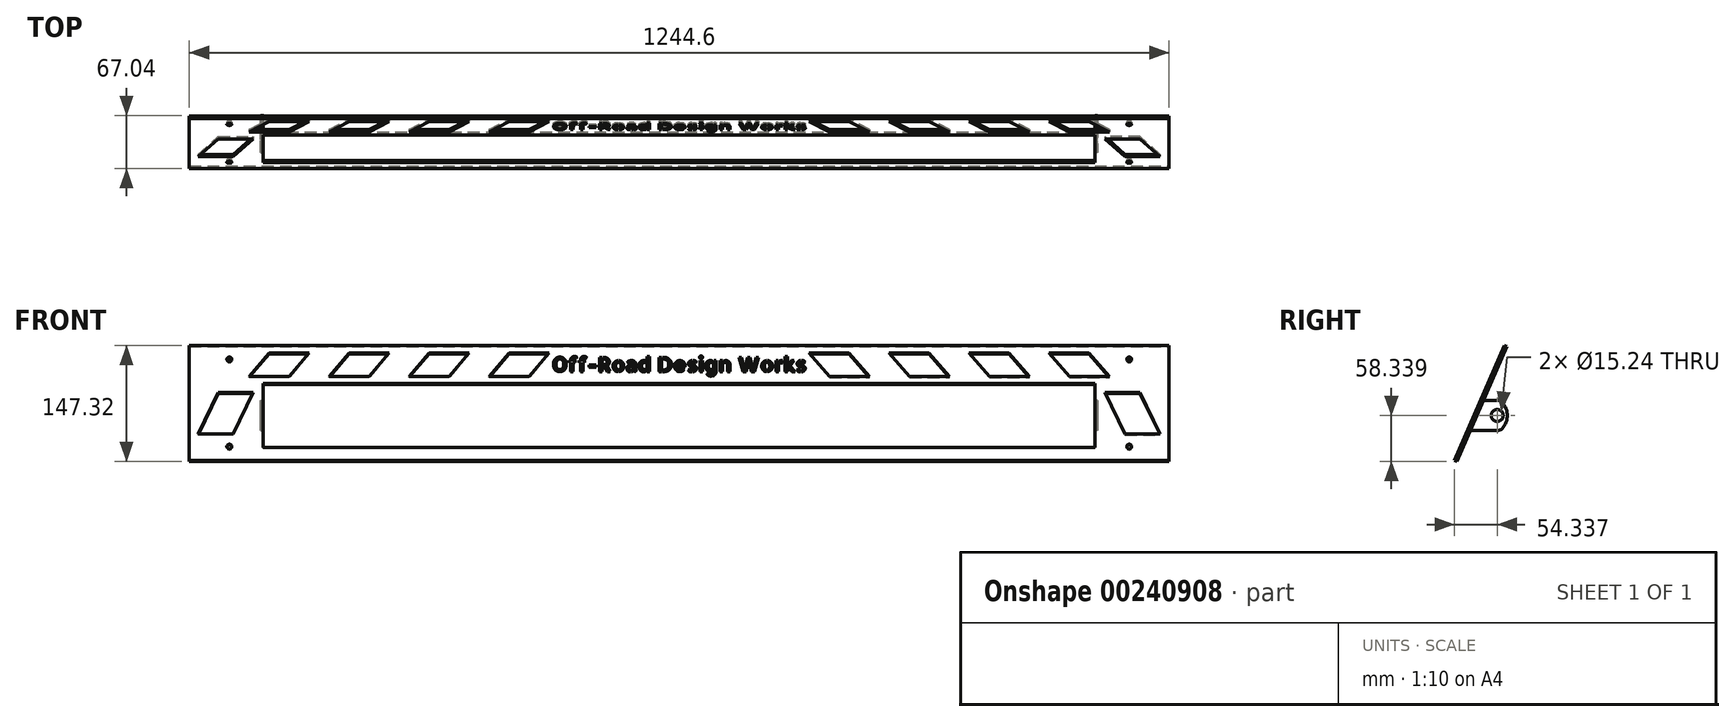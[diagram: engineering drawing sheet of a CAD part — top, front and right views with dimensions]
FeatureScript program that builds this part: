
annotation { "Feature Type Name" : "Feature", "Feature Type Description" : "" }
export const myFeature = defineFeature(function(context is Context, id is Id, definition is map)
    precondition{}
    {
        {
            var Q0;
            Q0=qCreatedBy(makeId("Right.planeOp"),FACE);
            var sketch = newSketch(context, id + "F0", { "sketchPlane" : qUnion([Q0])});
            skLineSegment(sketch, "E0", {"start": v(0, 0) * mm, "end": v(63.5, 146.05) * mm});
            skLineSegment(sketch, "E1", {"start": v(63.5, 146.05) * mm, "end": v(66.41, 144.78) * mm});
            skLineSegment(sketch, "E2", {"start": v(66.41, 144.78) * mm, "end": v(2.91, -1.27) * mm});
            skLineSegment(sketch, "E3", {"start": v(2.91, -1.27) * mm, "end": v(0, 0) * mm});
            skSolve(sketch);
        }
        {
            var Q0;
            Q0 = qSketchRegion(id + "F0", true);
            extrude(context, id + "F1", {"entities" : qUnion([Q0]), "oppositeDirection" : true, "depth" : 622.3 * mm, "hasSecondDirection" : true, "secondDirectionOppositeDirection" : false, "secondDirectionDepth" : 622.3 * mm});
        }
        {
            var Q0;
            Q0=makeQuery(id+"F1.opExtrude","SWEPT_FACE",FACE,{"disambiguationData":[OSD([sQuery(id+"F0.wireOp",EDGE,"E0")])]});
            var sketch = newSketch(context, id + "F2", { "sketchPlane" : qUnion([Q0])});
            skLineSegment(sketch, "E4", {"start": v(0, 0) * mm, "end": v(0, 463.2) * mm, "construction": true});
            skLineSegment(sketch, "E5", {"start": v(0, 106.68) * mm, "end": v(-528.32, 106.68) * mm});
            skLineSegment(sketch, "E6", {"start": v(-528.32, 106.68) * mm, "end": v(-528.32, 17.78) * mm});
            skLineSegment(sketch, "E7", {"start": v(-528.32, 17.78) * mm, "end": v(0, 17.78) * mm});
            skLineSegment(sketch, "E8.MirrorCS", {"start": v(0, 106.68) * mm, "end": v(528.32, 106.68) * mm});
            skLineSegment(sketch, "E9.MirrorCS", {"start": v(528.32, 106.68) * mm, "end": v(528.32, 17.78) * mm});
            skLineSegment(sketch, "E10.MirrorCS", {"start": v(528.32, 17.78) * mm, "end": v(0, 17.78) * mm});
            skLineSegment(sketch, "E11", {"start": v(165.1, 149.1) * mm, "end": v(215.9, 149.1) * mm});
            skLineSegment(sketch, "E12", {"start": v(215.9, 149.1) * mm, "end": v(241.7, 116.08) * mm});
            skLineSegment(sketch, "E13", {"start": v(241.7, 116.08) * mm, "end": v(190.9, 116.08) * mm});
            skLineSegment(sketch, "E14", {"start": v(190.9, 116.08) * mm, "end": v(165.1, 149.1) * mm});
            skLineSegment(sketch, "E15.1.0.0", {"start": v(317.5, 149.1) * mm, "end": v(343.3, 116.08) * mm});
            skLineSegment(sketch, "E15.1.0.1", {"start": v(343.3, 116.08) * mm, "end": v(292.5, 116.08) * mm});
            skLineSegment(sketch, "E15.1.0.2", {"start": v(266.7, 149.1) * mm, "end": v(317.5, 149.1) * mm});
            skLineSegment(sketch, "E15.1.0.3", {"start": v(292.5, 116.08) * mm, "end": v(266.7, 149.1) * mm});
            skLineSegment(sketch, "E15.2.0.0", {"start": v(419.1, 149.1) * mm, "end": v(444.9, 116.08) * mm});
            skLineSegment(sketch, "E15.2.0.1", {"start": v(444.9, 116.08) * mm, "end": v(394.1, 116.08) * mm});
            skLineSegment(sketch, "E15.2.0.2", {"start": v(368.3, 149.1) * mm, "end": v(419.1, 149.1) * mm});
            skLineSegment(sketch, "E15.2.0.3", {"start": v(394.1, 116.08) * mm, "end": v(368.3, 149.1) * mm});
            skLineSegment(sketch, "E15.3.0.0", {"start": v(520.7, 149.1) * mm, "end": v(546.5, 116.08) * mm});
            skLineSegment(sketch, "E15.3.0.1", {"start": v(546.5, 116.08) * mm, "end": v(495.7, 116.08) * mm});
            skLineSegment(sketch, "E15.3.0.2", {"start": v(469.9, 149.1) * mm, "end": v(520.7, 149.1) * mm});
            skLineSegment(sketch, "E15.3.0.3", {"start": v(495.7, 116.08) * mm, "end": v(469.9, 149.1) * mm});
            skLineSegment(sketch, "E15.direction1", {"start": v(215.9, 149.1) * mm, "end": v(317.5, 149.1) * mm, "construction": true});
            skLineSegment(sketch, "E16.MirrorCS", {"start": v(-190.9, 116.08) * mm, "end": v(-165.1, 149.1) * mm});
            skLineSegment(sketch, "E17.MirrorCS", {"start": v(-165.1, 149.1) * mm, "end": v(-215.9, 149.1) * mm});
            skLineSegment(sketch, "E18.MirrorCS", {"start": v(-215.9, 149.1) * mm, "end": v(-241.7, 116.08) * mm});
            skLineSegment(sketch, "E19.MirrorCS", {"start": v(-241.7, 116.08) * mm, "end": v(-190.9, 116.08) * mm});
            skLineSegment(sketch, "E20.MirrorCS", {"start": v(-292.5, 116.08) * mm, "end": v(-266.7, 149.1) * mm});
            skLineSegment(sketch, "E21.MirrorCS", {"start": v(-215.9, 149.1) * mm, "end": v(-317.5, 149.1) * mm, "construction": true});
            skLineSegment(sketch, "E22.MirrorCS", {"start": v(-317.5, 149.1) * mm, "end": v(-343.3, 116.08) * mm});
            skLineSegment(sketch, "E23.MirrorCS", {"start": v(-343.3, 116.08) * mm, "end": v(-292.5, 116.08) * mm});
            skLineSegment(sketch, "E24.MirrorCS", {"start": v(-394.1, 116.08) * mm, "end": v(-368.3, 149.1) * mm});
            skLineSegment(sketch, "E25.MirrorCS", {"start": v(-419.1, 149.1) * mm, "end": v(-444.9, 116.08) * mm});
            skLineSegment(sketch, "E26.MirrorCS", {"start": v(-368.3, 149.1) * mm, "end": v(-419.1, 149.1) * mm});
            skLineSegment(sketch, "E27.MirrorCS", {"start": v(-444.9, 116.08) * mm, "end": v(-394.1, 116.08) * mm});
            skLineSegment(sketch, "E28.MirrorCS", {"start": v(-495.7, 116.08) * mm, "end": v(-469.9, 149.1) * mm});
            skLineSegment(sketch, "E29.MirrorCS", {"start": v(-469.9, 149.1) * mm, "end": v(-520.7, 149.1) * mm});
            skLineSegment(sketch, "E30.MirrorCS", {"start": v(-520.7, 149.1) * mm, "end": v(-546.5, 116.08) * mm});
            skLineSegment(sketch, "E31.MirrorCS", {"start": v(-546.5, 116.08) * mm, "end": v(-495.7, 116.08) * mm});
            skLineSegment(sketch, "E32", {"start": v(-317.5, 149.1) * mm, "end": v(-266.7, 149.1) * mm});
            skCircle(sketch, "E33", {"center": v(571.5, 139.95) * mm, "radius": 3.18 * mm});
            skCircle(sketch, "E34", {"center": v(571.5, 19.3) * mm, "radius": 3.18 * mm});
            skCircle(sketch, "E35.MirrorC", {"center": v(-571.5, 139.95) * mm, "radius": 3.18 * mm});
            skCircle(sketch, "E36.MirrorC", {"center": v(-571.5, 19.3) * mm, "radius": 3.18 * mm});
            skSolve(sketch);
        }
        {
            var Q0;
            Q0 = qSketchRegion(id + "F2", true);
            var Q1;
            Q1=makeQuery(id+"F1.opExtrude","SWEPT_FACE",FACE,{"disambiguationData":[OSD([sQuery(id+"F0.wireOp",EDGE,"E2")])]});
            extrude(context, id + "F3", {"entities" : qUnion([Q0]), "operationType" : NewBodyOperationType.REMOVE, "endBound" : BoundingType.UP_TO_SURFACE, "oppositeDirection" : true, "endBoundEntityFace" : qUnion([Q1]), "depth" : 25.4 * mm});
        }
        {
            var Q0;
            Q0=makeQuery(id+"F3.boolean.opBoolean","COPY",FACE,{"derivedFrom":makeQuery(id+"F3.opExtrude","SWEPT_FACE",FACE,{"disambiguationData":[OSD([sQuery(id+"F2.wireOp",EDGE,"E6")])]})});
            var sketch = newSketch(context, id + "F4", { "sketchPlane" : qUnion([Q0])});
            skLineSegment(sketch, "E37", {"start": v(24.81, 57.07) * mm, "end": v(105.88, 57.07) * mm, "construction": true});
            skLineSegment(sketch, "E38", {"start": v(36.56, 76.12) * mm, "end": v(54.34, 76.12) * mm});
            skEllipticalArc(sketch, "E39", {});
            skLineSegment(sketch, "E40", {"start": v(54.34, 38.02) * mm, "end": v(20, 38.02) * mm});
            skCircle(sketch, "E41", {"center": v(54.34, 57.07) * mm, "radius": 7.62 * mm});
            skLineSegment(sketch, "E42", {"start": v(36.56, 76.12) * mm, "end": v(20, 38.02) * mm});
            const initialGuessF4  = {"E39": [0.054337447430503755, 0.05706926960064311, 0, 1, 0.01905, 0.0127, 3.141592653589793, 0]};
            skSetInitialGuess(sketch, initialGuessF4);
            skSolve(sketch);
        }
        {
            var Q0;
            Q0 = qSketchRegion(id + "F4", true);
            extrude(context, id + "F5", {"entities" : qUnion([Q0]), "operationType" : NewBodyOperationType.ADD, "oppositeDirection" : true, "depth" : 3.17 * mm});
        }
        {
            var Q0;
            Q0=makeQuery(id+"F3.boolean.opBoolean","COPY",FACE,{"derivedFrom":makeQuery(id+"F3.opExtrude","SWEPT_FACE",FACE,{"disambiguationData":[OSD([sQuery(id+"F2.wireOp",EDGE,"E9.MirrorCS")])]})});
            var sketch = newSketch(context, id + "F6", { "sketchPlane" : qUnion([Q0])});
            skLineSegment(sketch, "E43", {"start": v(-24.81, 57.07) * mm, "end": v(-133.24, 57.07) * mm, "construction": true});
            skLineSegment(sketch, "E44", {"start": v(-36.56, 76.12) * mm, "end": v(-54.34, 76.12) * mm});
            skEllipticalArc(sketch, "E45", {});
            skLineSegment(sketch, "E46", {"start": v(-54.34, 38.02) * mm, "end": v(-20, 38.02) * mm});
            skLineSegment(sketch, "E47", {"start": v(-20, 38.02) * mm, "end": v(-36.56, 76.12) * mm});
            skCircle(sketch, "E48", {"center": v(-54.34, 57.07) * mm, "radius": 7.62 * mm});
            const initialGuessF6  = {"E45": [-0.05433744743050189, 0.057069269600638836, 0, 1, 0.01905, 0.0127, 0, 3.141592653589793]};
            skSetInitialGuess(sketch, initialGuessF6);
            skSolve(sketch);
        }
        {
            var Q0;
            Q0 = qSketchRegion(id + "F6", true);
            extrude(context, id + "F7", {"entities" : qUnion([Q0]), "operationType" : NewBodyOperationType.ADD, "oppositeDirection" : true, "depth" : 3.17 * mm});
        }
        {
            var Q0;
            Q0=makeQuery(id+"F1.opExtrude","SWEPT_FACE",FACE,{"disambiguationData":[OSD([sQuery(id+"F0.wireOp",EDGE,"E0")])]});
            var sketch = newSketch(context, id + "F8", { "sketchPlane" : qUnion([Q0])});
            skText(sketch, "E49", { "text": "Off-Road Design Works", "fontName": "AllertaStencil-Regular.ttf"});
            skLineSegment(sketch, "E50", {"start": v(0, 123.19) * mm, "end": v(0, 72.97) * mm, "construction": true});
            const initialGuessF8  = {"E49": [-0.16193, 0.12319, 1, 0, 0.01955]};
            skSetInitialGuess(sketch, initialGuessF8);
            skSolve(sketch);
        }
        {
            var Q0;
            Q0 = qSketchRegion(id + "F8", true);
            var Q1;
            Q1=makeQuery(id+"F1.opExtrude","SWEPT_FACE",FACE,{"disambiguationData":[OSD([sQuery(id+"F0.wireOp",EDGE,"E2")])]});
            extrude(context, id + "F9", {"entities" : qUnion([Q0]), "operationType" : NewBodyOperationType.REMOVE, "endBound" : BoundingType.UP_TO_SURFACE, "oppositeDirection" : true, "endBoundEntityFace" : qUnion([Q1]), "depth" : 25.4 * mm});
        }
        {
            var Q0;
            Q0=makeQuery(id+"F1.opExtrude","SWEPT_FACE",FACE,{"disambiguationData":[OSD([sQuery(id+"F0.wireOp",EDGE,"E0")])]});
            var sketch = newSketch(context, id + "F10", { "sketchPlane" : qUnion([Q0])});
            skLineSegment(sketch, "E51", {"start": v(0, 0) * mm, "end": v(0, -145.22) * mm, "construction": true});
            skLineSegment(sketch, "E52", {"start": v(541.02, 93.98) * mm, "end": v(585.47, 93.98) * mm});
            skLineSegment(sketch, "E53", {"start": v(585.47, 93.98) * mm, "end": v(610.87, 36.83) * mm});
            skLineSegment(sketch, "E54", {"start": v(610.87, 36.83) * mm, "end": v(566.42, 36.83) * mm});
            skLineSegment(sketch, "E55", {"start": v(566.42, 36.83) * mm, "end": v(541.02, 93.98) * mm});
            skLineSegment(sketch, "E56.MirrorCS", {"start": v(-566.42, 36.83) * mm, "end": v(-541.02, 93.98) * mm});
            skLineSegment(sketch, "E57.MirrorCS", {"start": v(-541.02, 93.98) * mm, "end": v(-585.47, 93.98) * mm});
            skLineSegment(sketch, "E58.MirrorCS", {"start": v(-585.47, 93.98) * mm, "end": v(-610.87, 36.83) * mm});
            skLineSegment(sketch, "E59.MirrorCS", {"start": v(-610.87, 36.83) * mm, "end": v(-566.42, 36.83) * mm});
            skSolve(sketch);
        }
        {
            var Q0;
            Q0 = qSketchRegion(id + "F10", true);
            var Q1;
            Q1=makeQuery(id+"F1.opExtrude","SWEPT_FACE",FACE,{"disambiguationData":[OSD([sQuery(id+"F0.wireOp",EDGE,"E2")])]});
            extrude(context, id + "F11", {"entities" : qUnion([Q0]), "operationType" : NewBodyOperationType.REMOVE, "endBound" : BoundingType.UP_TO_SURFACE, "oppositeDirection" : true, "endBoundEntityFace" : qUnion([Q1]), "depth" : 25.4 * mm});
        }
    });
